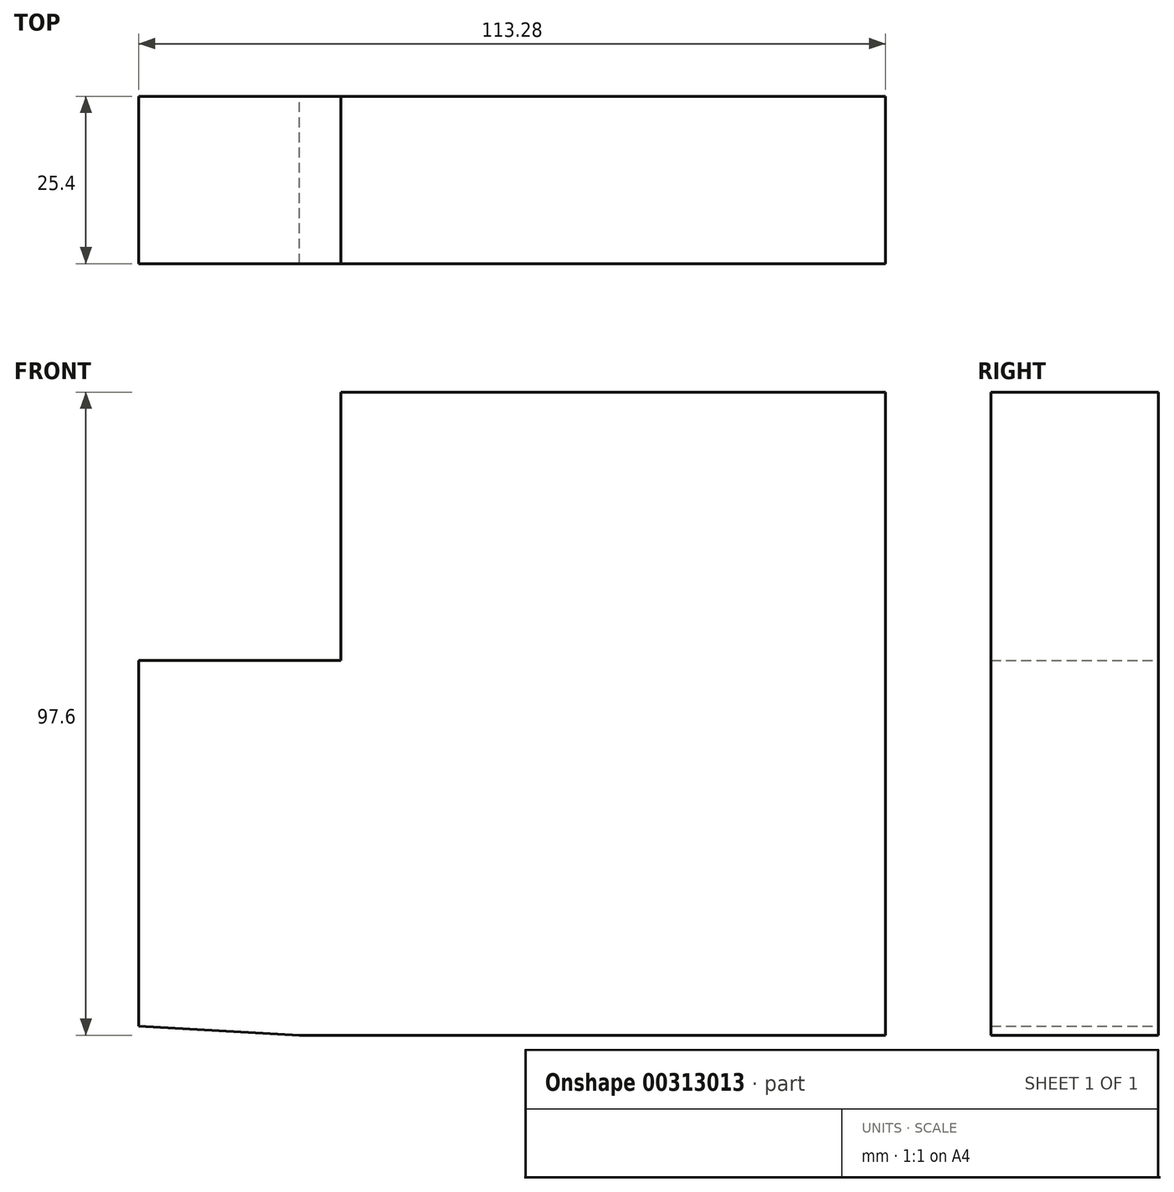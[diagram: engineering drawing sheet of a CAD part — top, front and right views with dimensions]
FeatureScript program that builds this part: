
annotation { "Feature Type Name" : "Feature", "Feature Type Description" : "" }
export const myFeature = defineFeature(function(context is Context, id is Id, definition is map)
    precondition{}
    {
        {
            var Q0;
            Q0=qCreatedBy(makeId("Front.planeOp"),FACE);
            var sketch = newSketch(context, id + "F0", { "sketchPlane" : qUnion([Q0])});
            skLineSegment(sketch, "E0", {"start": v(-50.83, -56.9) * mm, "end": v(38.07, -56.9) * mm});
            skLineSegment(sketch, "E1", {"start": v(38.07, -56.9) * mm, "end": v(38.07, -18.42) * mm});
            skLineSegment(sketch, "E2", {"start": v(38.07, -37.66) * mm, "end": v(38.07, -28.63) * mm});
            skLineSegment(sketch, "E3", {"start": v(38.07, -18.42) * mm, "end": v(38.07, 0) * mm});
            skLineSegment(sketch, "E4", {"start": v(38.07, 0) * mm, "end": v(38.07, 40.7) * mm});
            skLineSegment(sketch, "E5", {"start": v(38.07, 40.7) * mm, "end": v(-44.57, 40.7) * mm});
            skLineSegment(sketch, "E6", {"start": v(-44.57, 40.7) * mm, "end": v(-44.57, 0) * mm});
            skLineSegment(sketch, "E7", {"start": v(-44.57, 0) * mm, "end": v(-75.21, 0) * mm});
            skLineSegment(sketch, "E8", {"start": v(-75.21, 0) * mm, "end": v(-75.21, -55.56) * mm});
            skLineSegment(sketch, "E9", {"start": v(-75.21, -55.56) * mm, "end": v(-50.83, -56.9) * mm});
            skSolve(sketch);
        }
        {
            var Q0;
            Q0 = qSketchRegion(id + "F0", true);
            extrude(context, id + "F1", {"entities" : qUnion([Q0]), "depth" : 25.4 * mm});
        }
    });
